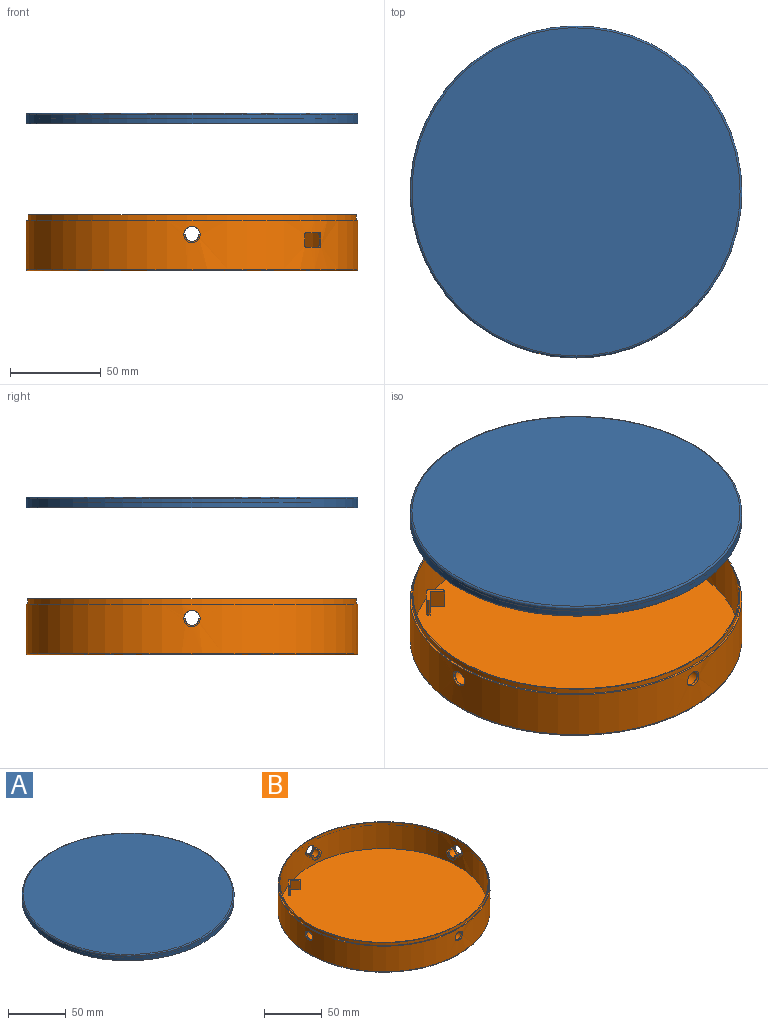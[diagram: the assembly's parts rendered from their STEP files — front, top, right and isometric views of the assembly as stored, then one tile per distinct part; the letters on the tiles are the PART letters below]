
ASSEMBLY  parts=2 mates=1
PART A: 6 faces, bbox 198.1x198.1x6 mm
  f0: cylinder r=91.5mm len=183mm, axis (0,0,-1), area 2874.6mm2, adj f2,f4
  f1: plane 181x181mm, normal (0,0,1), area 25730.4mm2, adj f2
  f2: torus R=90.5mm, axis (0,0,1), area 899.5mm2, adj f0,f1
  f3: cylinder r=91mm len=182mm, axis (0,0,1), area 1715.3mm2, adj f4,f5
  f4: plane 183x183mm, normal (0,0,-1), area 286.7mm2, adj f0,f3
  f5: plane 182x182mm, normal (0,0,-1), area 26015.5mm2, adj f3
PART B: 68 faces, bbox 198.1x198.1x31 mm
  f0: cylinder r=90mm len=180mm, axis (0,0,1), area 15413.7mm2, adj f2,f5,f6,f7,f8,f10,f11,f12
  f1: cylinder r=91.5mm len=183mm, axis (0,0,1), area 15164.6mm2, adj f4,f5,f6,f7,f8,f9,f58,f59
  f2: plane 180x180mm, normal (0,0,1), area 25376.2mm2, adj f0,f38,f39,f40,f41,f42,f43,f44
  f3: plane 181x181mm, normal (0,0,-1), area 25730.4mm2, adj f9
  f4: plane 183x183mm, normal (0,0,1), area 571.8mm2, adj f1,f66
  f5: cylinder r=4.5mm len=9mm, axis (0,-1,0), area 42.4mm2, adj f0,f1
  f6: cylinder r=4.5mm len=9mm, axis (0,-1,0), area 42.4mm2, adj f0,f1
  f7: cylinder r=4.5mm len=9mm, axis (1,0,0), area 42.4mm2, adj f0,f1
  f8: cylinder r=4.5mm len=9mm, axis (1,0,0), area 42.4mm2, adj f0,f1
  f9: torus R=90.5mm, axis (0,0,1), area 899.5mm2, adj f1,f3
  f10: plane 7.86x2.2mm, normal (0,0,1), area 8.4mm2, adj f0,f11,f13,f14,f15,f16
  f11: cylinder r=5.9mm len=11.81mm, axis (-1,0,0), area 146.5mm2, adj f0,f10,f12,f14
  f12: plane 7.86x2.2mm, normal (0,0,1), area 8.4mm2, adj f0,f11,f13,f14,f15,f16
  f13: cylinder r=5mm len=10mm, axis (-1,0,0), area 108.9mm2, adj f0,f10,f12,f16
  f14: plane 11.81x5.9mm, normal (-1,0,0), area 33.2mm2, adj f10,f11,f12,f15
  f15: cylinder r=3.7mm len=7.4mm, axis (-1,0,0), area 11.6mm2, adj f10,f12,f14,f16
  f16: plane 10x5mm, normal (1,0,0), area 17.8mm2, adj f10,f12,f13,f15
  f17: plane 7.86x2.2mm, normal (0,0,1), area 8.4mm2, adj f0,f18,f20,f21,f22,f23
  f18: cylinder r=5.9mm len=11.81mm, axis (1,0,0), area 146.5mm2, adj f0,f17,f19,f21
  f19: plane 7.86x2.2mm, normal (0,0,1), area 8.4mm2, adj f0,f18,f20,f21,f22,f23
  f20: cylinder r=5mm len=10mm, axis (1,0,0), area 108.9mm2, adj f0,f17,f19,f23
  f21: plane 11.81x5.9mm, normal (1,0,0), area 33.2mm2, adj f17,f18,f19,f22
  f22: cylinder r=3.7mm len=7.4mm, axis (1,0,0), area 11.6mm2, adj f17,f19,f21,f23
  f23: plane 10x5mm, normal (-1,0,0), area 17.8mm2, adj f17,f19,f20,f22
  f24: plane 7.86x2.2mm, normal (0,0,1), area 8.4mm2, adj f0,f25,f27,f28,f29,f30
  f25: cylinder r=5.9mm len=11.81mm, axis (0,1,0), area 146.5mm2, adj f0,f24,f26,f28
  f26: plane 7.86x2.2mm, normal (0,0,1), area 8.4mm2, adj f0,f25,f27,f28,f29,f30
  f27: cylinder r=5mm len=10mm, axis (0,1,0), area 108.9mm2, adj f0,f24,f26,f30
  f28: plane 11.81x5.9mm, normal (0,1,0), area 33.2mm2, adj f24,f25,f26,f29
  f29: cylinder r=3.7mm len=7.4mm, axis (0,1,0), area 11.6mm2, adj f24,f26,f28,f30
  f30: plane 10x5mm, normal (0,-1,0), area 17.8mm2, adj f24,f26,f27,f29
  f31: plane 7.86x2.2mm, normal (0,0,1), area 8.4mm2, adj f0,f32,f34,f35,f36,f37
  f32: cylinder r=5.9mm len=11.81mm, axis (0,-1,0), area 146.5mm2, adj f0,f31,f33,f35
  f33: plane 7.86x2.2mm, normal (0,0,1), area 8.4mm2, adj f0,f32,f34,f35,f36,f37
  f34: cylinder r=5mm len=10mm, axis (0,-1,0), area 108.9mm2, adj f0,f31,f33,f37
  f35: plane 11.81x5.9mm, normal (0,-1,0), area 33.2mm2, adj f31,f32,f33,f36
  f36: cylinder r=3.7mm len=7.4mm, axis (0,-1,0), area 11.6mm2, adj f31,f33,f35,f37
  f37: plane 10x5mm, normal (0,1,0), area 17.8mm2, adj f31,f33,f34,f36
  f38: plane 10x5.66mm, normal (0.71,-0.71,0), area 80mm2, adj f2,f39,f46,f47
  f39: plane 10x0.71mm, normal (0.71,0.71,0), area 10mm2, adj f2,f38,f40,f47
  f40: cylinder r=1mm len=10mm, axis (0,0,-1), area 15.7mm2, adj f2,f39,f41,f47
  f41: plane 10x5.66mm, normal (-0.71,0.71,0), area 80mm2, adj f2,f40,f42,f47
  f42: cylinder r=1mm len=10mm, axis (0,0,-1), area 15.7mm2, adj f2,f41,f43,f47
  f43: plane 10x5.66mm, normal (-0.71,-0.71,0), area 80mm2, adj f2,f42,f44,f47
  f44: cylinder r=1mm len=10mm, axis (0,0,-1), area 15.7mm2, adj f2,f43,f45,f47
  f45: plane 10x0.71mm, normal (0.71,-0.71,0), area 10mm2, adj f2,f44,f46,f47
  f46: plane 10x5.66mm, normal (0.71,0.71,0), area 80mm2, adj f2,f38,f45,f47
  f47: plane 13.31x8.07mm, normal (0,0,1), area 35.4mm2, adj f38,f39,f40,f41,f42,f43,f44,f45
  f48: plane 10x0.71mm, normal (0.71,-0.71,0), area 10mm2, adj f2,f49,f56,f57
  f49: cylinder r=1mm len=10mm, axis (0,0,-1), area 15.7mm2, adj f2,f48,f50,f57
  f50: plane 10x5.66mm, normal (0.71,0.71,0), area 80mm2, adj f2,f49,f51,f57
  f51: cylinder r=1mm len=10mm, axis (0,0,-1), area 15.7mm2, adj f2,f50,f52,f57
  f52: plane 10x5.66mm, normal (-0.71,0.71,0), area 80mm2, adj f2,f51,f53,f57
  f53: cylinder r=1mm len=10mm, axis (0,0,-1), area 15.7mm2, adj f2,f52,f54,f57
  f54: plane 10x0.71mm, normal (-0.71,-0.71,0), area 10mm2, adj f2,f53,f55,f57
  f55: plane 10x5.66mm, normal (0.71,-0.71,0), area 80mm2, adj f2,f54,f56,f57
  f56: plane 10x5.66mm, normal (-0.71,-0.71,0), area 80mm2, adj f2,f48,f55,f57
  f57: plane 13.31x8.07mm, normal (0,0,1), area 35.4mm2, adj f48,f49,f50,f51,f52,f53,f54,f55
  f58: plane 6x1.07mm, normal (-0.71,-0.71,0), area 9.1mm2, adj f0,f1,f59,f65
  f59: cylinder r=1mm len=1.84mm, axis (-0.71,0.71,0), area 2.4mm2, adj f0,f1,f58,f60
  f60: plane 9.1x8.58mm, normal (0,0,-1), area 16.5mm2, adj f0,f1,f59,f61
  f61: cylinder r=1mm len=1.79mm, axis (-0.71,0.71,0), area 2.4mm2, adj f0,f1,f60,f62
  f62: plane 6x1.06mm, normal (0.71,0.71,0), area 9mm2, adj f0,f1,f61,f63
  f63: cylinder r=1mm len=1.79mm, axis (-0.71,0.71,0), area 2.4mm2, adj f0,f1,f62,f64
  f64: plane 9.1x8.58mm, normal (0,0,1), area 16.5mm2, adj f0,f1,f63,f65
  f65: cylinder r=1mm len=1.84mm, axis (-0.71,0.71,0), area 2.4mm2, adj f0,f1,f58,f64
  f66: cylinder r=90.5mm len=181mm, axis (0,0,-1), area 1705.9mm2, adj f4,f67
  f67: plane 181x181mm, normal (0,0,1), area 283.5mm2, adj f0,f66
PLACE A t=(3.52,32.38,56.08)mm
PLACE B t=(3.52,32.38,0)mm
MATE slider A.f0 <-> B.f1  axis (0,0,1) through (3.52,32.38,59.08)mm
